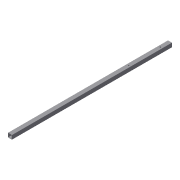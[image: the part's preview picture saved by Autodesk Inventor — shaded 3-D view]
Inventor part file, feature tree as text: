
AUTODESK INVENTOR PART (.ipt)
format: ipt  version: 2017 (Build 210142000, 142)  size: 113,152 bytes
history: native  units: in
note: dims shown in document units (in); Inventor stores cm internally (conversion verified against a paired STEP export)
features: other x7, sketch x3, reference x3, hole x2, extrude x1
ambient origin geometry x8: Origin, YZ Plane, XZ Plane, XY Plane, X Axis, Y Axis, Z Axis, Center Point
bodies: Solid1 (feature_tree)
feature tree (16):
  extrude  "Extrusion1"  Depth=0.748in
  hole  "Hole1"  [1 undecoded]
  hole  "Hole2"  [1 undecoded]
  sketch  "Sketch2"  dims[d0=0.748in d1=0.748in]
  sketch  "Sketch3"  dims[d2=0.063in d3=0.0098in]
  reference  "Reference1"
  reference  "Reference2"
  sketch  "Sketch5"  dims[d4=29.9213in d5=0.0in d6=0.2165in d7=0.75in d8=0.375in d9=0.25in d10=0.5635in d11=1.0in d12=0.8108in d13=0.2362in d14=0.75in d15=0.375in d16=0.25in d17=0.5635in d18=1.0in d19=0.8108in]
  reference  "Reference3"
  other  "<userpath>\Google Drive\HERA\hera-cad\feed\bpSupAssy37\bpSupAssy37.iam"
  other  "bpSupAssy37.iam"
  other  "bpSparJig:1"
  other  "<userpath>\Google Drive\HERA\hera-cad\feed\bpSupAssembly.iam"
  other  "bpSupAssembly.iam"
  other  "bpMechSupAssembly:1"
  other  "bpSupInner1:2"
note: 2 required parameter values undecoded (feature->parameter linkage not recoverable at this tier; creation-order binding heuristic only, values carry confidence <= 0.55)
